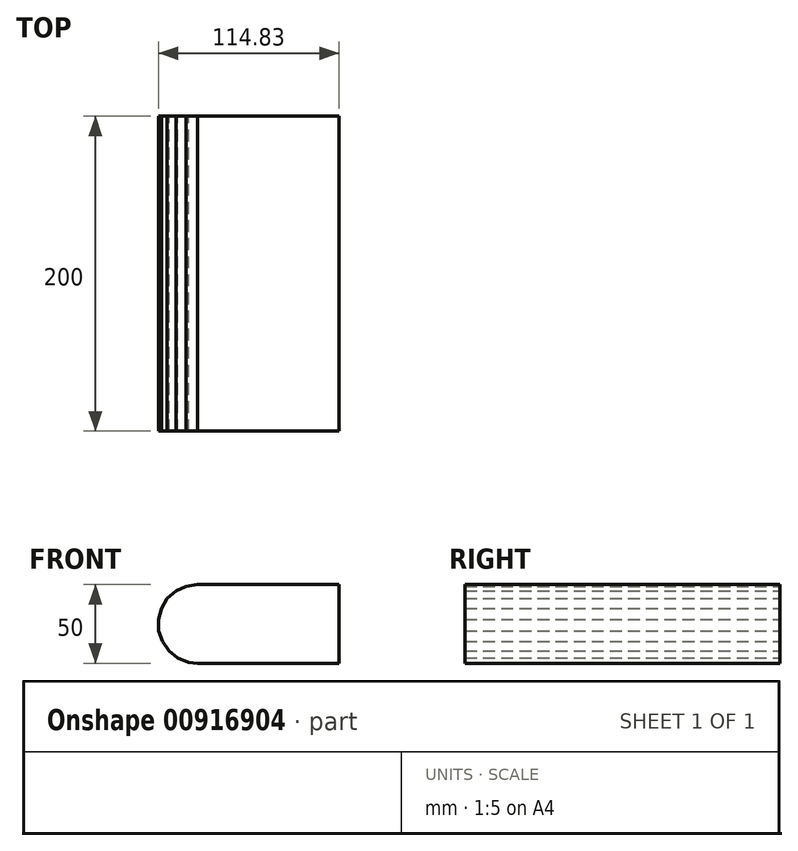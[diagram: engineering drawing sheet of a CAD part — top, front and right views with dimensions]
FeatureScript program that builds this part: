
annotation { "Feature Type Name" : "Feature", "Feature Type Description" : "" }
export const myFeature = defineFeature(function(context is Context, id is Id, definition is map)
    precondition{}
    {
        {
            var Q0;
            Q0=qCreatedBy(makeId("Front.planeOp"),FACE);
            var sketch = newSketch(context, id + "F0", { "sketchPlane" : qUnion([Q0])});
            skLineSegment(sketch, "E0.bottom", {"start": v(0, 0) * mm, "end": v(-90, 0) * mm});
            skLineSegment(sketch, "E0.top", {"start": v(0, 50) * mm, "end": v(-90, 50) * mm});
            skLineSegment(sketch, "E0.left", {"start": v(0, 0) * mm, "end": v(0, 50) * mm});
            skLineSegment(sketch, "E0.right", {"start": v(-90, 0) * mm, "end": v(-90, 50) * mm, "construction": true});
            skCircle(sketch, "E1", {"center": v(-90, 25) * mm, "radius": 25 * mm, "construction": true});
            skCircle(sketch, "E2", {"center": v(-90, 50) * mm, "radius": 7.25 * mm, "construction": true});
            skCircle(sketch, "E3", {"center": v(-97.17, 48.95) * mm, "radius": 7.25 * mm, "construction": true});
            skCircle(sketch, "E4", {"center": v(-103.74, 45.88) * mm, "radius": 7.25 * mm, "construction": true});
            skCircle(sketch, "E5", {"center": v(-109.16, 41.06) * mm, "radius": 7.25 * mm, "construction": true});
            skCircle(sketch, "E6", {"center": v(-112.96, 34.89) * mm, "radius": 7.25 * mm, "construction": true});
            skCircle(sketch, "E7", {"center": v(-114.83, 27.89) * mm, "radius": 7.25 * mm, "construction": true});
            skCircle(sketch, "E8", {"center": v(-114.62, 20.64) * mm, "radius": 7.25 * mm, "construction": true});
            skCircle(sketch, "E9", {"center": v(-112.33, 13.76) * mm, "radius": 7.25 * mm, "construction": true});
            skCircle(sketch, "E10", {"center": v(-108.17, 7.82) * mm, "radius": 7.25 * mm, "construction": true});
            skCircle(sketch, "E11", {"center": v(-102.47, 3.33) * mm, "radius": 7.25 * mm, "construction": true});
            skCircle(sketch, "E12", {"center": v(-95.73, 0.67) * mm, "radius": 7.25 * mm, "construction": true});
            skLineSegment(sketch, "E13", {"start": v(-90, 50) * mm, "end": v(-97.17, 48.95) * mm});
            skLineSegment(sketch, "E14", {"start": v(-103.74, 45.88) * mm, "end": v(-97.17, 48.95) * mm});
            skLineSegment(sketch, "E15", {"start": v(-103.74, 45.88) * mm, "end": v(-109.16, 41.06) * mm});
            skLineSegment(sketch, "E16", {"start": v(-109.16, 41.06) * mm, "end": v(-112.96, 34.89) * mm});
            skLineSegment(sketch, "E17", {"start": v(-112.96, 34.89) * mm, "end": v(-114.83, 27.89) * mm});
            skLineSegment(sketch, "E18", {"start": v(-114.83, 27.89) * mm, "end": v(-114.62, 20.64) * mm});
            skLineSegment(sketch, "E19", {"start": v(-114.62, 20.64) * mm, "end": v(-112.33, 13.76) * mm});
            skLineSegment(sketch, "E20", {"start": v(-112.33, 13.76) * mm, "end": v(-108.17, 7.82) * mm});
            skLineSegment(sketch, "E21", {"start": v(-108.17, 7.82) * mm, "end": v(-102.47, 3.33) * mm});
            skLineSegment(sketch, "E22", {"start": v(-102.47, 3.33) * mm, "end": v(-95.73, 0.67) * mm});
            skLineSegment(sketch, "E23", {"start": v(-95.73, 0.67) * mm, "end": v(-90, 0) * mm});
            skSolve(sketch);
        }
        {
            var Q0;
            Q0 = qSketchRegion(id + "F0", true);
            extrude(context, id + "F1", {"entities" : qUnion([Q0]), "depth" : 200 * mm, "offsetDistance" : 25 * mm});
        }
    });
